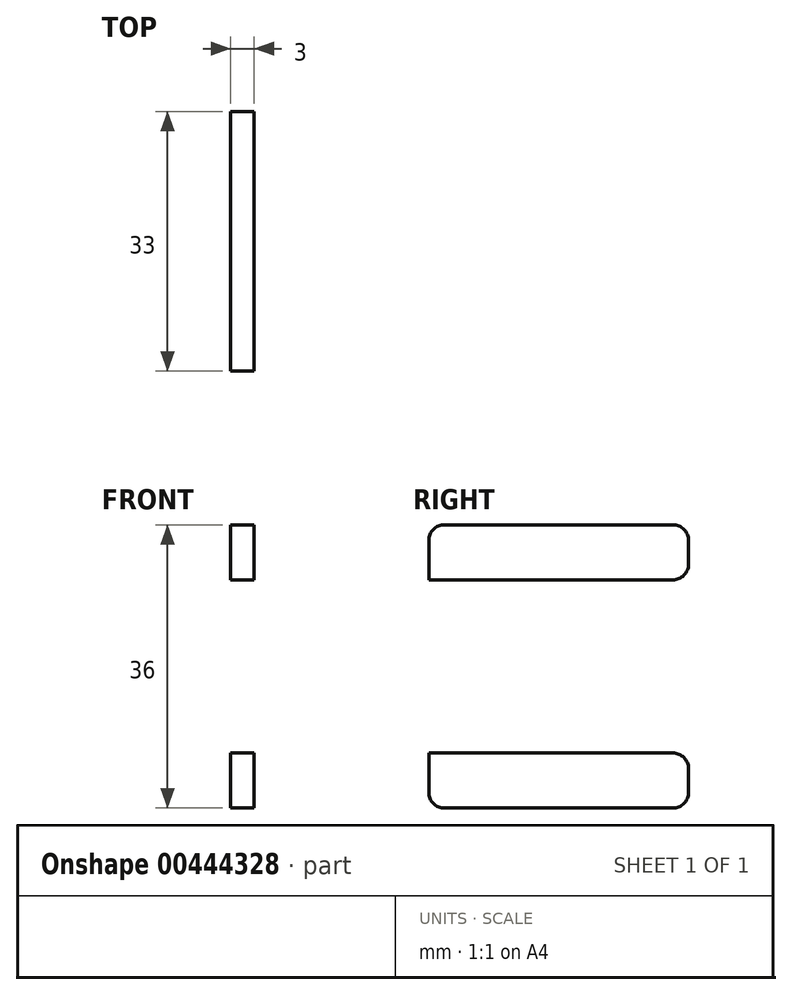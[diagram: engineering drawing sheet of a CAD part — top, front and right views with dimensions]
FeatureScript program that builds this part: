
annotation { "Feature Type Name" : "Feature", "Feature Type Description" : "" }
export const myFeature = defineFeature(function(context is Context, id is Id, definition is map)
    precondition{}
    {
        {
            var Q0;
            Q0=qCreatedBy(makeId("Right.planeOp"),FACE);
            var sketch = newSketch(context, id + "F0", { "sketchPlane" : qUnion([Q0])});
            skLineSegment(sketch, "E0.bottom", {"start": v(0, 0) * mm, "end": v(33, 0) * mm});
            skLineSegment(sketch, "E0.top", {"start": v(0, 7) * mm, "end": v(33, 7) * mm});
            skLineSegment(sketch, "E0.left", {"start": v(0, 0) * mm, "end": v(0, 7) * mm});
            skLineSegment(sketch, "E0.right", {"start": v(33, 0) * mm, "end": v(33, 7) * mm});
            skLineSegment(sketch, "E1.bottom", {"start": v(0, 7) * mm, "end": v(7, 7) * mm});
            skLineSegment(sketch, "E1.top", {"start": v(0, 29) * mm, "end": v(7, 29) * mm});
            skLineSegment(sketch, "E1.left", {"start": v(0, 7) * mm, "end": v(0, 29) * mm});
            skLineSegment(sketch, "E1.right", {"start": v(7, 7) * mm, "end": v(7, 29) * mm});
            skLineSegment(sketch, "E2.bottom", {"start": v(0, 29) * mm, "end": v(33, 29) * mm});
            skLineSegment(sketch, "E2.top", {"start": v(0, 36) * mm, "end": v(33, 36) * mm});
            skLineSegment(sketch, "E2.left", {"start": v(0, 29) * mm, "end": v(0, 36) * mm});
            skLineSegment(sketch, "E2.right", {"start": v(33, 29) * mm, "end": v(33, 36) * mm});
            skSolve(sketch);
        }
        {
            var Q0;
            Q0=makeQuery(id+"F0.imprint","IMPRINT",FACE,{"disambiguationData":[TD([[makeQuery(id+"F0.imprint","IMPRINT",EDGE,{"derivedFrom":sQuery(id+"F0.wireOp",EDGE,"E2.top")}),-1.0]])]});
            var Q1;
            Q1=makeQuery(id+"F0.imprint","IMPRINT",FACE,{"disambiguationData":[TD([[makeQuery(id+"F0.imprint","IMPRINT",EDGE,{"derivedFrom":sQuery(id+"F0.wireOp",EDGE,"E1.bottom")}),1.0]])]});
            var Q2;
            Q2=makeQuery(id+"F0.imprint","IMPRINT",FACE,{"disambiguationData":[TD([[makeQuery(id+"F0.imprint","IMPRINT",EDGE,{"derivedFrom":sQuery(id+"F0.wireOp",EDGE,"E0.bottom")}),1.0]])]});
            extrude(context, id + "F1", {"entities" : qUnion([Q0, Q1, Q2]), "depth" : 3 * mm});
        }
        {
            var Q0;
            Q0=makeQuery(id+"F1.opExtrude","SWEPT_EDGE",EDGE,{"disambiguationData":[OSD([sQuery(id+"F0.wireOp",EDGE,"E2.top"),sQuery(id+"F0.wireOp",EDGE,"E2.right")])]});
            var Q1;
            Q1=makeQuery(id+"F1.opExtrude","SWEPT_EDGE",EDGE,{"disambiguationData":[OSD([sQuery(id+"F0.wireOp",EDGE,"E0.top"),sQuery(id+"F0.wireOp",EDGE,"E0.right")])]});
            var Q2;
            Q2=makeQuery(id+"F1.opExtrude","SWEPT_EDGE",EDGE,{"disambiguationData":[OSD([sQuery(id+"F0.wireOp",EDGE,"E2.bottom"),sQuery(id+"F0.wireOp",EDGE,"E2.right")])]});
            var Q3;
            Q3=makeQuery(id+"F1.opExtrude","SWEPT_EDGE",EDGE,{"disambiguationData":[OSD([sQuery(id+"F0.wireOp",EDGE,"E0.bottom"),sQuery(id+"F0.wireOp",EDGE,"E0.right")])]});
            var Q4;
            Q4=makeQuery(id+"F1.opExtrude","SWEPT_EDGE",EDGE,{"disambiguationData":[OSD([sQuery(id+"F0.wireOp",EDGE,"E0.bottom"),sQuery(id+"F0.wireOp",EDGE,"E0.left")])]});
            var Q5;
            Q5=makeQuery(id+"F1.opExtrude","SWEPT_EDGE",EDGE,{"disambiguationData":[OSD([sQuery(id+"F0.wireOp",EDGE,"E2.top"),sQuery(id+"F0.wireOp",EDGE,"E2.left")])]});
            var Q6;
            Q6=makeQuery(id+"F1.opExtrude","SWEPT_EDGE",EDGE,{"disambiguationData":[OSD([sQuery(id+"F0.wireOp",EDGE,"E0.top"),sQuery(id+"F0.wireOp",EDGE,"E1.bottom"),sQuery(id+"F0.wireOp",EDGE,"E1.right")])]});
            var Q7;
            Q7=makeQuery(id+"F1.opExtrude","SWEPT_EDGE",EDGE,{"disambiguationData":[OSD([sQuery(id+"F0.wireOp",EDGE,"E1.right"),sQuery(id+"F0.wireOp",EDGE,"E2.bottom")])]});
            fillet(context, id + "F2", {"entities" : qUnion([Q0, Q1, Q2, Q3, Q4, Q5, Q6, Q7]), "radius" : 2 * mm, "tangentPropagation" : true, "allowEdgeOverflow" : false});
        }
    });
